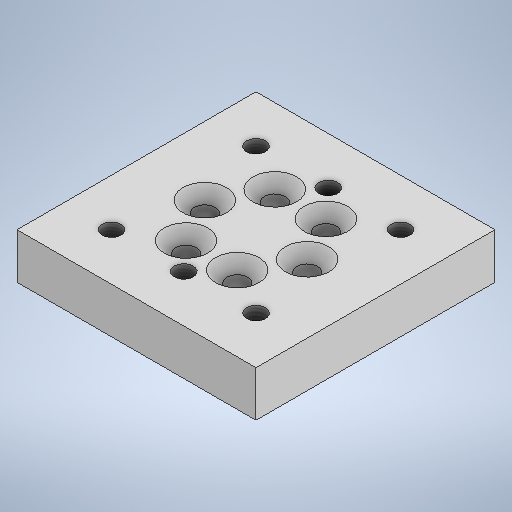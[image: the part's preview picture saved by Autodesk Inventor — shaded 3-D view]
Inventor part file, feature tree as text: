
AUTODESK INVENTOR PART (.ipt)
format: ipt  version: 2025 (Build 290162000, 162)  size: 285,184 bytes
history: native  units: mm
features: thread x6, sketch x4, extrude x2, chamfer x1
ambient origin geometry x8: Origin, YZ Plane, XZ Plane, XY Plane, X Axis, Y Axis, Z Axis, Center Point
bodies: Solid1 (feature_tree)
feature tree (13):
  extrude  "Extrusion1"  Depth=63.0mm
  extrude  "Extrusion2"  Depth=31.5mm
  chamfer  "Chamfer1"  Distance=19.05mm
  thread  "Thread2"  [1 undecoded]
  thread  "Thread3"  [1 undecoded]
  thread  "Thread4"  [1 undecoded]
  thread  "Thread5"  [1 undecoded]
  thread  "Thread6"  [1 undecoded]
  thread  "Thread7"  [1 undecoded]
  sketch  "Sketch1"  dims[d0=63.0mm d1=63.0mm]
  sketch  "Sketch Rectangular Pattern1"  dims[d2=6.2mm d3=31.5mm]
  sketch  "Sketch2"  dims[d5=19.05mm d6=19.05mm d7=5.0mm d8=30.0mm d10=19.05mm d11=20.0mm d13=38.1mm d16=12.0mm d17=0.0mm d18=5.5mm d19=13.5mm d20=0.0mm d21=60.0mm d23=360.0deg d25=12.0mm d26=0.0mm d29=3.0mm d30=2.0mm d31=45.0deg d35=12.0mm d36=0.0mm d37=12.0mm d38=0.0mm d39=12.0mm d40=0.0mm d41=12.0mm d42=0.0mm d43=12.0mm d44=0.0mm d45=12.0mm d46=0.0mm]
  sketch  "Sketch Circular Pattern1"  dims[d4=31.5mm]
note: 6 required parameter values undecoded (feature->parameter linkage not recoverable at this tier; creation-order binding heuristic only, values carry confidence <= 0.55)
